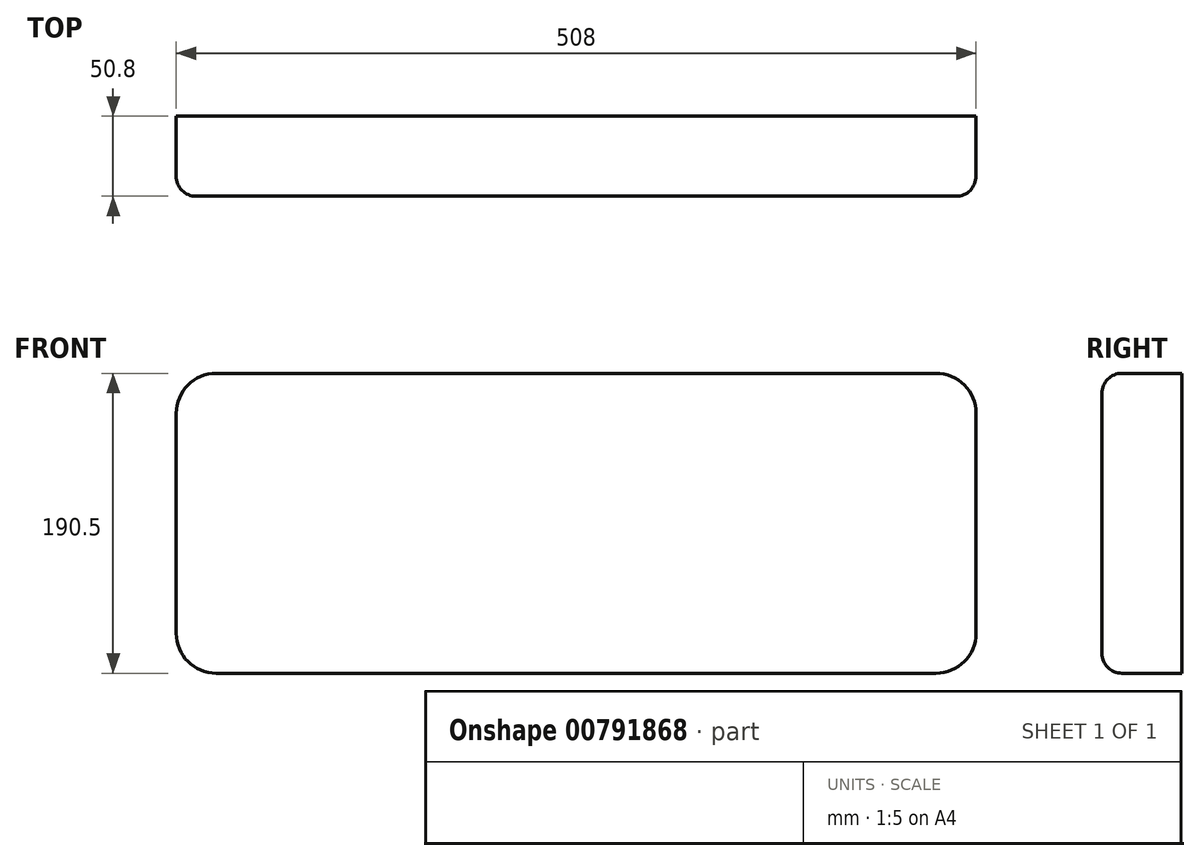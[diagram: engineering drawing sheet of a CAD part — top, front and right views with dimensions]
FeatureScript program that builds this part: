
annotation { "Feature Type Name" : "Feature", "Feature Type Description" : "" }
export const myFeature = defineFeature(function(context is Context, id is Id, definition is map)
    precondition{}
    {
        {
            var Q0;
            Q0=qCreatedBy(makeId("Front.planeOp"),FACE);
            var sketch = newSketch(context, id + "F0", { "sketchPlane" : qUnion([Q0])});
            skLineSegment(sketch, "E0.bottom", {"start": v(0, 0) * mm, "end": v(508, 0) * mm});
            skLineSegment(sketch, "E0.top", {"start": v(0, 190.5) * mm, "end": v(508, 190.5) * mm});
            skLineSegment(sketch, "E0.left", {"start": v(0, 0) * mm, "end": v(0, 190.5) * mm});
            skLineSegment(sketch, "E0.right", {"start": v(508, 0) * mm, "end": v(508, 190.5) * mm});
            skSolve(sketch);
        }
        {
            var Q0;
            Q0 = qSketchRegion(id + "F0", true);
            extrude(context, id + "F1", {"entities" : qUnion([Q0]), "oppositeDirection" : true, "depth" : 50.8 * mm, "offsetDistance" : 25.4 * mm});
        }
        {
            var Q0;
            Q0=makeQuery(id+"F1.opExtrude","SWEPT_EDGE",EDGE,{"disambiguationData":[OSD([sQuery(id+"F0.wireOp",EDGE,"E0.top"),sQuery(id+"F0.wireOp",EDGE,"E0.left")])]});
            var Q1;
            Q1=makeQuery(id+"F1.opExtrude","SWEPT_EDGE",EDGE,{"disambiguationData":[OSD([sQuery(id+"F0.wireOp",EDGE,"E0.top"),sQuery(id+"F0.wireOp",EDGE,"E0.right")])]});
            var Q2;
            Q2=makeQuery(id+"F1.opExtrude","SWEPT_EDGE",EDGE,{"disambiguationData":[OSD([sQuery(id+"F0.wireOp",EDGE,"E0.bottom"),sQuery(id+"F0.wireOp",EDGE,"E0.right")])]});
            var Q3;
            Q3=makeQuery(id+"F1.opExtrude","SWEPT_EDGE",EDGE,{"disambiguationData":[OSD([sQuery(id+"F0.wireOp",EDGE,"E0.bottom"),sQuery(id+"F0.wireOp",EDGE,"E0.left")])]});
            fillet(context, id + "F2", {"entities" : qUnion([Q0, Q1, Q2, Q3]), "radius" : 25.4 * mm, "tangentPropagation" : true, "allowEdgeOverflow" : false});
        }
        {
            var Q0;
            Q0=makeQuery(id+"F1.opExtrude","CAP_EDGE",EDGE,{"disambiguationData":[OSD([sQuery(id+"F0.wireOp",EDGE,"E0.top")])],"isStart":true});
            fillet(context, id + "F3", {"entities" : qUnion([Q0]), "radius" : 12.7 * mm, "tangentPropagation" : true, "allowEdgeOverflow" : false});
        }
    });
